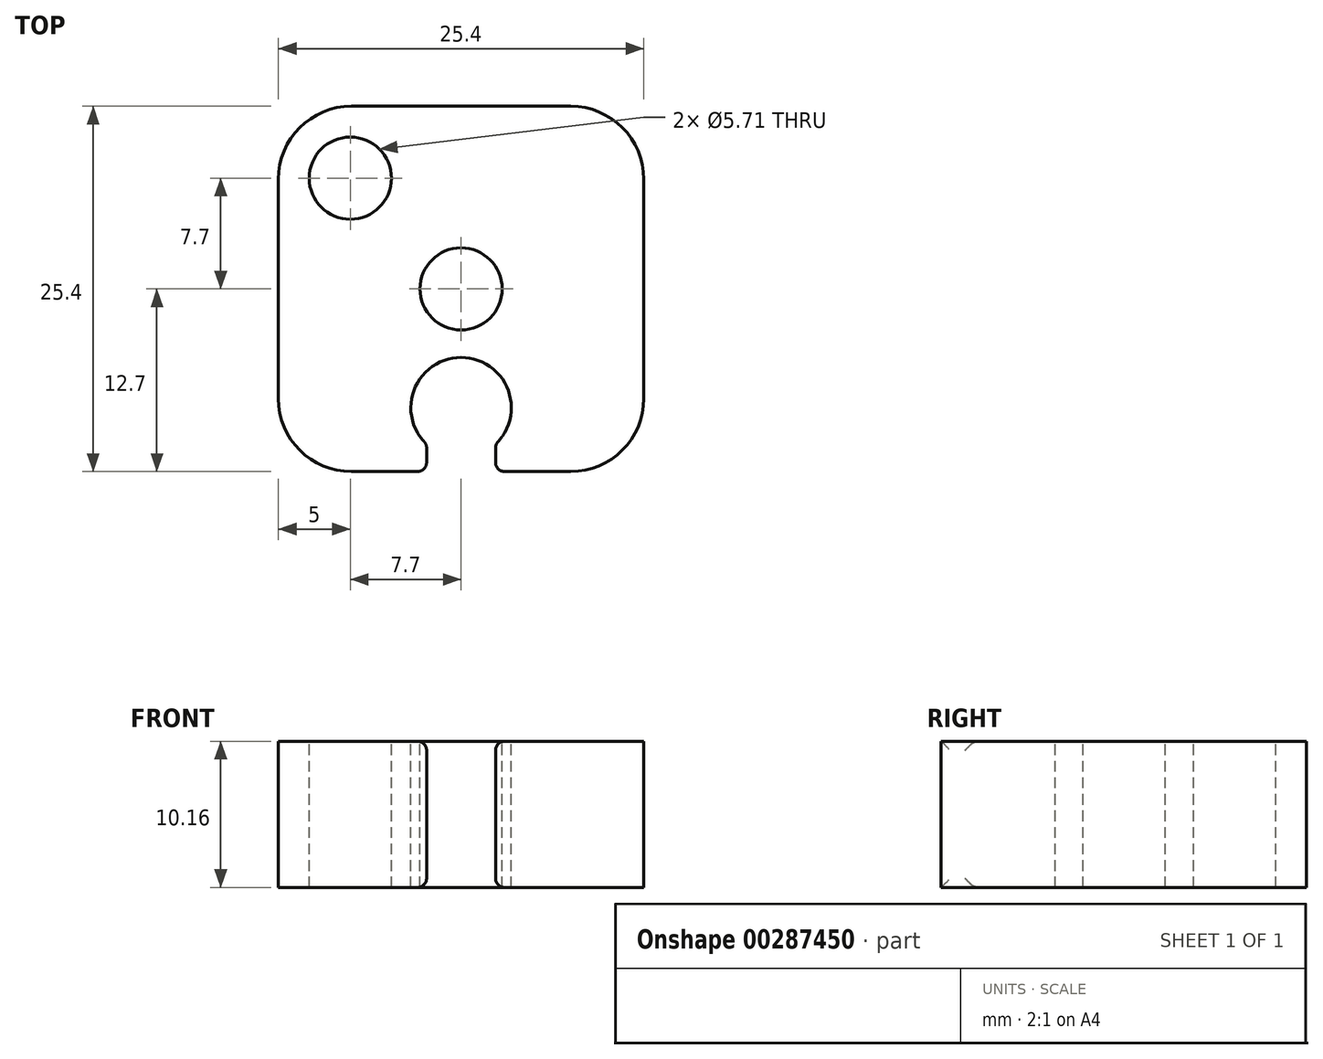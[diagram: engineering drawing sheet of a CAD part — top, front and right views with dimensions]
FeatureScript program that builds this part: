
annotation { "Feature Type Name" : "Feature", "Feature Type Description" : "" }
export const myFeature = defineFeature(function(context is Context, id is Id, definition is map)
    precondition{}
    {
        {
            var Q0;
            Q0=qCreatedBy(makeId("Top.planeOp"),FACE);
            var sketch = newSketch(context, id + "F0", { "sketchPlane" : qUnion([Q0])});
            skLineSegment(sketch, "E0.bottom", {"start": v(12.7, -12.7) * mm, "end": v(-12.7, -12.7) * mm});
            skLineSegment(sketch, "E0.top", {"start": v(12.7, 12.7) * mm, "end": v(-12.7, 12.7) * mm});
            skLineSegment(sketch, "E0.left", {"start": v(12.7, -12.7) * mm, "end": v(12.7, 12.7) * mm});
            skLineSegment(sketch, "E0.right", {"start": v(-12.7, -12.7) * mm, "end": v(-12.7, 12.7) * mm});
            skPoint(sketch, "E0.middle", {"position": v(0, 0) * mm});
            skSolve(sketch);
        }
        {
            var Q0;
            Q0=qSketchRegion(id+"F0",true);
            extrude(context, id + "F1", {"entities" : qUnion([Q0]), "depth" : 10.16 * mm});
        }
        {
            var Q0;
            Q0=makeQuery(id+"F1.opExtrude","CAP_FACE",FACE,{"disambiguationData":[OSD([sQuery(id+"F0.wireOp",EDGE,"E0.bottom"),sQuery(id+"F0.wireOp",EDGE,"E0.top"),sQuery(id+"F0.wireOp",EDGE,"E0.left"),sQuery(id+"F0.wireOp",EDGE,"E0.right")])],"isStart":false});
            var sketch = newSketch(context, id + "F2", { "sketchPlane" : qUnion([Q0])});
            skCircle(sketch, "E1", {"center": v(0, -8.26) * mm, "radius": 3.5 * mm});
            skSolve(sketch);
        }
        {
            var Q0;
            Q0=qSketchRegion(id+"F2",true);
            extrude(context, id + "F3", {"entities" : qUnion([Q0]), "operationType" : NewBodyOperationType.REMOVE, "oppositeDirection" : true, "depth" : 25.4 * mm});
        }
        {
            var Q0;
            Q0=makeQuery(id+"F1.opExtrude","CAP_FACE",FACE,{"disambiguationData":[OSD([sQuery(id+"F0.wireOp",EDGE,"E0.bottom"),sQuery(id+"F0.wireOp",EDGE,"E0.top"),sQuery(id+"F0.wireOp",EDGE,"E0.left"),sQuery(id+"F0.wireOp",EDGE,"E0.right")])],"isStart":false});
            var sketch = newSketch(context, id + "F4", { "sketchPlane" : qUnion([Q0])});
            skLineSegment(sketch, "E2.bottom", {"start": v(-2.4, -12.7) * mm, "end": v(2.4, -12.7) * mm});
            skLineSegment(sketch, "E2.top", {"start": v(-2.4, -10.8) * mm, "end": v(2.4, -10.8) * mm, "construction": true});
            skLineSegment(sketch, "E2.left", {"start": v(-2.4, -12.7) * mm, "end": v(-2.4, -10.8) * mm});
            skLineSegment(sketch, "E2.right", {"start": v(2.4, -12.7) * mm, "end": v(2.4, -10.8) * mm});
            skLineSegment(sketch, "E3", {"start": v(-2.4, -11.75) * mm, "end": v(0, -11.75) * mm, "construction": true});
            skLineSegment(sketch, "E4", {"start": v(0, -11.75) * mm, "end": v(0, -10.8) * mm, "construction": true});
            skArc(sketch, "E5", {"start": v(-2.4, -10.8) * mm, "mid": v(0, -11.75) * mm, "end": v(2.4, -10.8) * mm});
            skSolve(sketch);
        }
        {
            var Q0;
            Q0=makeQuery(id+"F4.imprint","IMPRINT",FACE,{"disambiguationData":[TD([[makeQuery(id+"F4.imprint","IMPRINT",EDGE,{"derivedFrom":sQuery(id+"F4.wireOp",EDGE,"E2.bottom")}),-1.0]])]});
            extrude(context, id + "F5", {"entities" : qUnion([Q0]), "operationType" : NewBodyOperationType.REMOVE, "oppositeDirection" : true, "depth" : 25.4 * mm});
        }
        {
            var Q0;
            Q0=qCreatedBy(makeId("Front.planeOp"),FACE);
            var sketch = newSketch(context, id + "F6", { "sketchPlane" : qUnion([Q0])});
            skLineSegment(sketch, "E6", {"start": v(0, 0) * mm, "end": v(0, 12.7) * mm, "construction": true});
            skSolve(sketch);
        }
        {
            var Q0;
            Q0=makeQuery(id+"F1.opExtrude","CAP_FACE",FACE,{"disambiguationData":[OSD([sQuery(id+"F0.wireOp",EDGE,"E0.bottom"),sQuery(id+"F0.wireOp",EDGE,"E0.top"),sQuery(id+"F0.wireOp",EDGE,"E0.left"),sQuery(id+"F0.wireOp",EDGE,"E0.right")])],"isStart":false});
            var sketch = newSketch(context, id + "F7", { "sketchPlane" : qUnion([Q0])});
            skCircle(sketch, "E7", {"center": v(0, 0) * mm, "radius": 2.86 * mm});
            skSolve(sketch);
        }
        {
            var Q0;
            Q0=makeQuery(id+"F7.imprint","IMPRINT",FACE,{"disambiguationData":[TD([[makeQuery(id+"F7.imprint","IMPRINT",EDGE,{"derivedFrom":sQuery(id+"F7.wireOp",EDGE,"E7")}),1.0]])]});
            extrude(context, id + "F8", {"entities" : qUnion([Q0]), "operationType" : NewBodyOperationType.REMOVE, "oppositeDirection" : true, "depth" : 25.4 * mm});
        }
        {
            var Q0;
            Q0=makeQuery(id+"F1.opExtrude","CAP_FACE",FACE,{"disambiguationData":[OSD([sQuery(id+"F0.wireOp",EDGE,"E0.bottom"),sQuery(id+"F0.wireOp",EDGE,"E0.top"),sQuery(id+"F0.wireOp",EDGE,"E0.left"),sQuery(id+"F0.wireOp",EDGE,"E0.right")])],"isStart":false});
            var sketch = newSketch(context, id + "F9", { "sketchPlane" : qUnion([Q0])});
            skCircle(sketch, "E8", {"center": v(-7.7, 7.7) * mm, "radius": 2.86 * mm});
            skSolve(sketch);
        }
        {
            var Q0;
            Q0=makeQuery(id+"F9.imprint","IMPRINT",FACE,{"disambiguationData":[TD([[makeQuery(id+"F9.imprint","IMPRINT",EDGE,{"derivedFrom":sQuery(id+"F9.wireOp",EDGE,"E8")}),1.0]])]});
            extrude(context, id + "F10", {"entities" : qUnion([Q0]), "operationType" : NewBodyOperationType.REMOVE, "oppositeDirection" : true, "depth" : 25.4 * mm});
        }
        {
            var Q0;
            Q0=makeQuery(id+"F1.opExtrude","SWEPT_EDGE",EDGE,{"disambiguationData":[OSD([sQuery(id+"F0.wireOp",EDGE,"E0.top"),sQuery(id+"F0.wireOp",EDGE,"E0.right")])]});
            var Q1;
            Q1=makeQuery(id+"F1.opExtrude","SWEPT_EDGE",EDGE,{"disambiguationData":[OSD([sQuery(id+"F0.wireOp",EDGE,"E0.bottom"),sQuery(id+"F0.wireOp",EDGE,"E0.right")])]});
            var Q2;
            Q2=makeQuery(id+"F1.opExtrude","SWEPT_EDGE",EDGE,{"disambiguationData":[OSD([sQuery(id+"F0.wireOp",EDGE,"E0.bottom"),sQuery(id+"F0.wireOp",EDGE,"E0.left")])]});
            var Q3;
            Q3=makeQuery(id+"F1.opExtrude","SWEPT_EDGE",EDGE,{"disambiguationData":[OSD([sQuery(id+"F0.wireOp",EDGE,"E0.top"),sQuery(id+"F0.wireOp",EDGE,"E0.left")])]});
            fillet(context, id + "F11", {"entities" : qUnion([Q0, Q1, Q2, Q3]), "radius" : 5.08 * mm, "tangentPropagation" : true, "allowEdgeOverflow" : false});
        }
        {
            var Q0;
            Q0=makeQuery(id+"FBK2ZA7MzFuvV71_1.2.F5.boolean.opBoolean","COPY",FACE,{"derivedFrom":makeQuery(id+"FBK2ZA7MzFuvV71_1.2.F5.opExtrude","SWEPT_FACE",FACE,{"disambiguationData":[OSD([sQuery(id+"F4.wireOp",EDGE,"E2.right")])]})});
            var Q1;
            Q1=makeQuery(id+"FBK2ZA7MzFuvV71_1.2.F5.boolean.opBoolean","COPY",FACE,{"derivedFrom":makeQuery(id+"FBK2ZA7MzFuvV71_1.2.F5.opExtrude","SWEPT_FACE",FACE,{"disambiguationData":[OSD([sQuery(id+"F4.wireOp",EDGE,"E2.left")])]})});
            var Q2;
            Q2=makeQuery(id+"FBK2ZA7MzFuvV71_1.3.F5.boolean.opBoolean","COPY",FACE,{"derivedFrom":makeQuery(id+"FBK2ZA7MzFuvV71_1.3.F5.opExtrude","SWEPT_FACE",FACE,{"disambiguationData":[OSD([sQuery(id+"F4.wireOp",EDGE,"E2.right")])]})});
            var Q3;
            Q3=makeQuery(id+"FBK2ZA7MzFuvV71_1.3.F5.boolean.opBoolean","COPY",FACE,{"derivedFrom":makeQuery(id+"FBK2ZA7MzFuvV71_1.3.F5.opExtrude","SWEPT_FACE",FACE,{"disambiguationData":[OSD([sQuery(id+"F4.wireOp",EDGE,"E2.left")])]})});
            var Q4;
            Q4=makeQuery(id+"F5.boolean.opBoolean","COPY",FACE,{"derivedFrom":makeQuery(id+"F5.opExtrude","SWEPT_FACE",FACE,{"disambiguationData":[OSD([sQuery(id+"F4.wireOp",EDGE,"E2.right")])]})});
            var Q5;
            Q5=makeQuery(id+"F5.boolean.opBoolean","COPY",FACE,{"derivedFrom":makeQuery(id+"F5.opExtrude","SWEPT_FACE",FACE,{"disambiguationData":[OSD([sQuery(id+"F4.wireOp",EDGE,"E2.left")])]})});
            var Q6;
            Q6=makeQuery(id+"FBK2ZA7MzFuvV71_1.1.F5.boolean.opBoolean","COPY",FACE,{"derivedFrom":makeQuery(id+"FBK2ZA7MzFuvV71_1.1.F5.opExtrude","SWEPT_FACE",FACE,{"disambiguationData":[OSD([sQuery(id+"F4.wireOp",EDGE,"E2.right")])]})});
            var Q7;
            Q7=makeQuery(id+"FBK2ZA7MzFuvV71_1.1.F5.boolean.opBoolean","COPY",FACE,{"derivedFrom":makeQuery(id+"FBK2ZA7MzFuvV71_1.1.F5.opExtrude","SWEPT_FACE",FACE,{"disambiguationData":[OSD([sQuery(id+"F4.wireOp",EDGE,"E2.left")])]})});
            fillet(context, id + "F12", {"entities" : qUnion([Q0, Q1, Q2, Q3, Q4, Q5, Q6, Q7]), "radius" : 0.64 * mm, "tangentPropagation" : true, "allowEdgeOverflow" : false});
        }
    });
